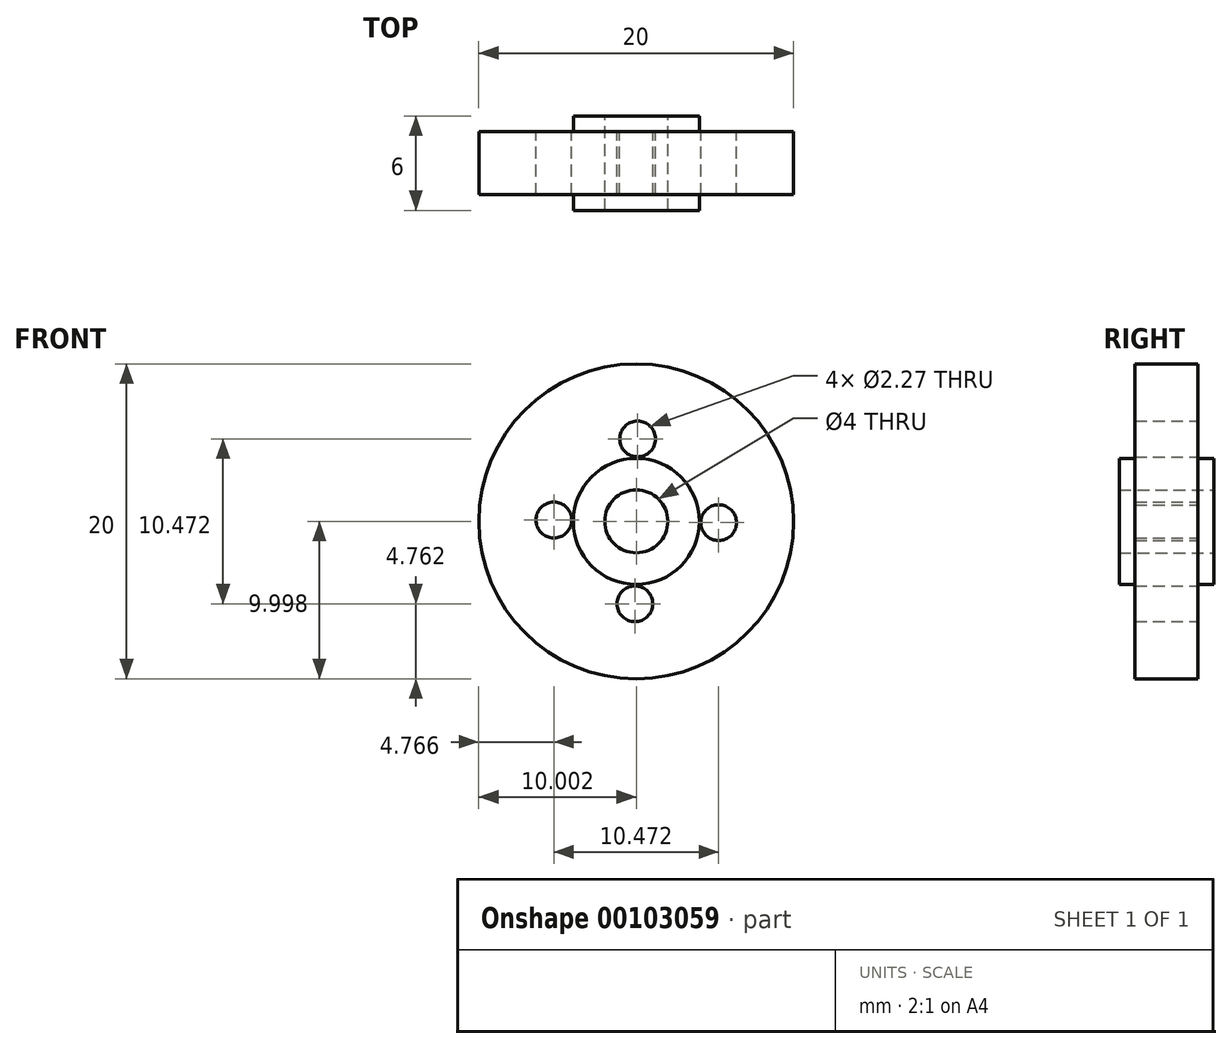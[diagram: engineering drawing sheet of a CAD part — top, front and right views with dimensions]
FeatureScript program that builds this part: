
annotation { "Feature Type Name" : "Feature", "Feature Type Description" : "" }
export const myFeature = defineFeature(function(context is Context, id is Id, definition is map)
    precondition{}
    {
        {
            var Q0;
            Q0=qCreatedBy(makeId("Front.planeOp"),FACE);
            var sketch = newSketch(context, id + "F0", { "sketchPlane" : qUnion([Q0])});
            skCircle(sketch, "E0", {"center": v(-53.44, 43.3) * mm, "radius": 10 * mm});
            skCircle(sketch, "E1", {"center": v(-53.44, 43.3) * mm, "radius": 2 * mm});
            skCircle(sketch, "E2", {"center": v(-53.35, 48.54) * mm, "radius": 1.14 * mm});
            skCircle(sketch, "E3.1.0", {"center": v(-58.67, 43.4) * mm, "radius": 1.14 * mm});
            skCircle(sketch, "E3.2.0", {"center": v(-53.52, 38.07) * mm, "radius": 1.14 * mm});
            skCircle(sketch, "E3.3.0", {"center": v(-48.2, 43.22) * mm, "radius": 1.14 * mm});
            skCircle(sketch, "E4", {"center": v(-53.44, 43.3) * mm, "radius": 4 * mm});
            skSolve(sketch);
        }
        {
            var Q0;
            Q0=makeQuery(id+"F0.imprint","IMPRINT",FACE,{"disambiguationData":[TD([[makeQuery(id+"F0.imprint","IMPRINT",EDGE,{"derivedFrom":sQuery(id+"F0.wireOp",EDGE,"E0")}),1.0]])]});
            extrude(context, id + "F1", {"entities" : qUnion([Q0]), "endBound" : BoundingType.SYMMETRIC, "depth" : 4 * mm});
        }
        {
            var Q0;
            Q0=makeQuery(id+"F0.imprint","IMPRINT",FACE,{"disambiguationData":[TD([[makeQuery(id+"F0.imprint","IMPRINT",EDGE,{"derivedFrom":sQuery(id+"F0.wireOp",EDGE,"E1")}),-1.0]])]});
            extrude(context, id + "F2", {"entities" : qUnion([Q0]), "operationType" : NewBodyOperationType.ADD, "endBound" : BoundingType.SYMMETRIC, "depth" : 6 * mm});
        }
    });
